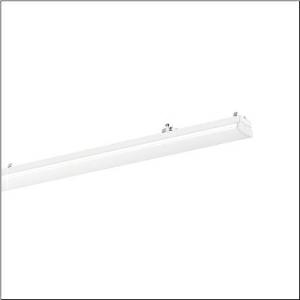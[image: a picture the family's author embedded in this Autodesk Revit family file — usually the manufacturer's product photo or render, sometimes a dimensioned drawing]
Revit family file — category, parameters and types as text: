
# Revit family: licross_21_recessed_opal_mo_52tl1dmn36xg
name_source: partatom
category: Lighting Fixtures
units: mm (PartAtom-declared; Revit-internal decimal feet)

## family parameters
Cut with Voids When Loaded = No
Host = Face
Light Source = No
Part Type = Normal
Room Calculation Point = No
Round Connector Dimension = Use Diameter
Shared = No

## types (1)
- --- (1 x LED, 6300 lm, 37.5 W, 3000K)
    Apparent Load = 38 VA
    CIE Flux Codes = 44 73 91 87 100
    Color Rendering = 80
    Color Temperature = 3000K
    Default Elevation = 1800 mm
    Description = Licross 21 recessed opal MO, luminaire insert, of sheet steel, galvanised, coil coated, white, length: 1.500mm, width: 66mm, height: 67mm, LED rated luminous flux: 6.300lm, light colour: 830, SDCM (Standard Deviation of Colour Matching)MacAdam ≤ 3 SDCM (initial), control gear: ON/OFF Multilumen, with plug, 3-pole, with phase selection, mains connection: 220..240V, AC, 50/60Hz, rated input power: 37.5W, internal wiring halogen-free, primary optical cover: cover, of PMMA, light emission: direct with ceiling illumination distribution, primary light characteristic: symmetric, protection rating (complete): IP40, insulation class (complete): insulation class I (protective earthing), certification: CE, ENEC, VDE, UKCA, protection symbol: D if used in an environment without relevant dust loads with corresponding accessories, impact resistance: IK06, permissible ambient temperature for indoor applications: -35..+50°C, corresponds to IFS (International Featured Standards) requirements for safety and quality in the food industry, reducing of maximum allowable ambient temperature of 5°C with ceiling mounting, LABS conformity tested according to VDMA 24364:2018-05, The light source and the operating device comply with the requirements of the Ecodesign Regulation (EU) 2019/2020 and are replaceable in accordance with this regulation, packaging unit: 1 piece
    Height = 83 mm
    Lamp = 1 x LED
    Lamp Light Flux = 6300 lm
    Lamp Power = 37.5 W
    Lamp count = 1
    Length = 1500 mm
    Luminous efficacy = 168 lm/W
    Manufacturer = Siteco
    ModVariant = No
    Model = 52TL1DMN36XG
    Mounting Place = Ceiling
    Mounting Type = Pendant
    Number of Poles = 1
    OnlyDefault = Yes
    Power Factor = 1
    Product Name = Licross 21 recessed opal MO
    Product group = luminaire insert | ceiling pendant
    ProductGroupID = 901
    Protection Class = Protection class I
    Protection Degree = IP 40
    RLX_Detail_Level = 1
    RLX_Emergency_Light_Flux = 0 lm
    RLX_Emergency_Type = 0
    RLX_Emergency_Type_DB = No
    RlxData = <blob elided: 24773 chars, md5=58e70def>
    Socket = socket
    Standby Power = 0 W
    System Light Flux = 6300 lm
    System Power = 38 W
    Type Comments = factory setting: luminous flux: 100 % | (A | C | E) | 87 mA
    Type Image = l_1313666.jpg
    URL = http://relux.com
    VarID = @adj_029921
    Voltage = 0 V
    Weight = 0.00 kg
    Width = 76 mm

## geometry (parser evidence)
native form markers: Blend x4, Sweep x12
no freeform markers — native parametric forms only
